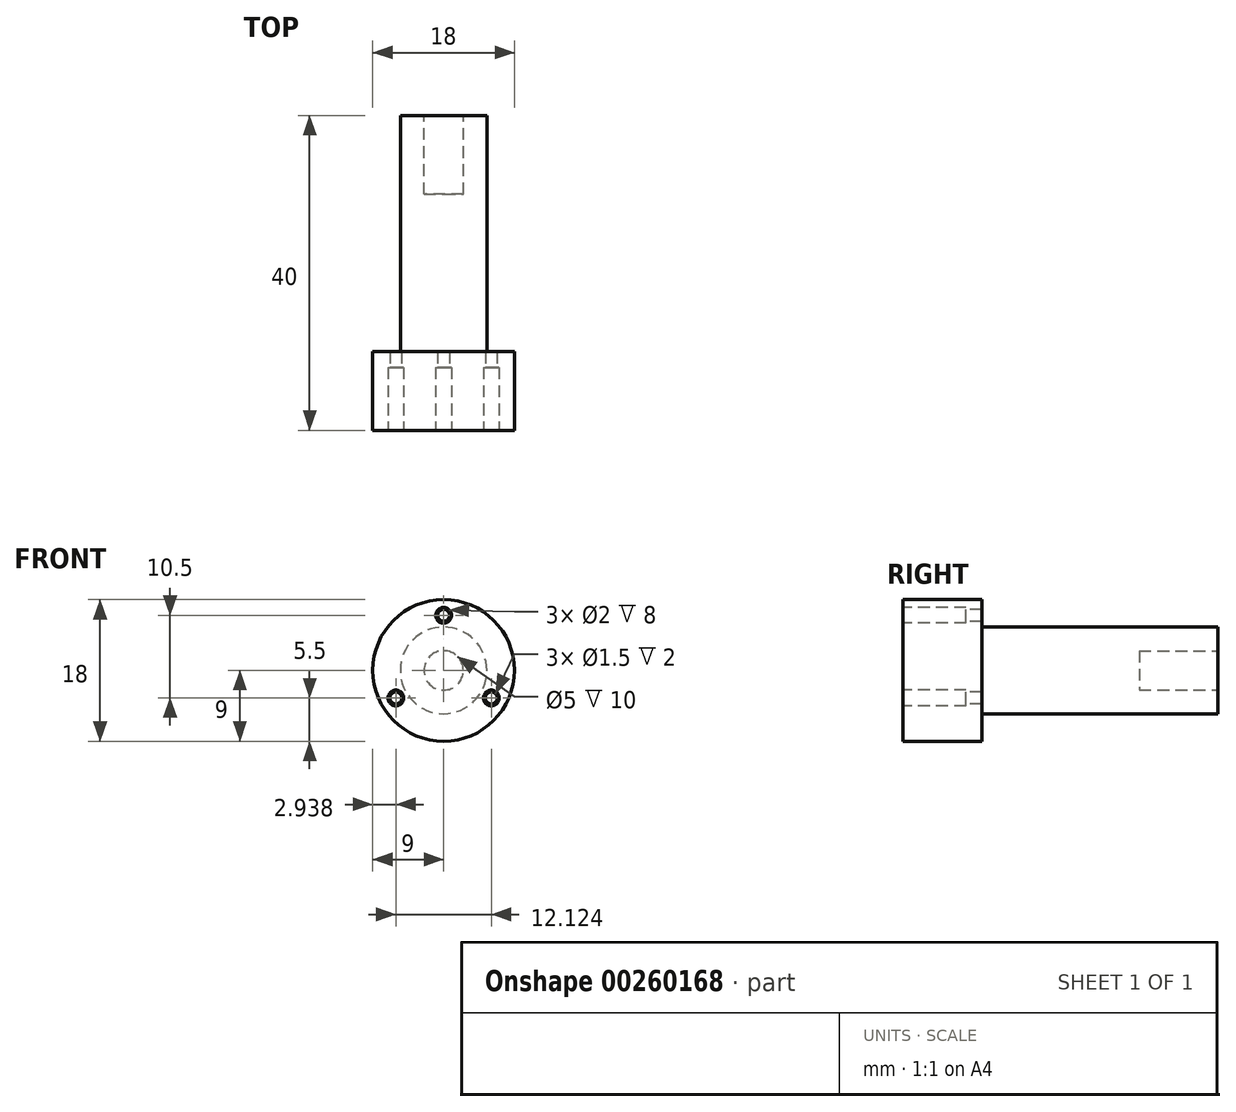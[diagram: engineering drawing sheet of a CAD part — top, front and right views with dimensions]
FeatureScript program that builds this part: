
annotation { "Feature Type Name" : "Feature", "Feature Type Description" : "" }
export const myFeature = defineFeature(function(context is Context, id is Id, definition is map)
    precondition{}
    {
        {
            var Q0;
            Q0=qCreatedBy(makeId("Front.planeOp"),FACE);
            var sketch = newSketch(context, id + "F0", { "sketchPlane" : qUnion([Q0])});
            skCircle(sketch, "E0", {"center": v(0, 0) * mm, "radius": 9 * mm});
            skSolve(sketch);
        }
        {
            var Q0;
            Q0=makeQuery(id+"F0.imprint","IMPRINT",FACE,{"disambiguationData":[TD([[makeQuery(id+"F0.imprint","IMPRINT",EDGE,{"derivedFrom":sQuery(id+"F0.wireOp",EDGE,"E0")}),1.0]])]});
            extrude(context, id + "F1", {"entities" : qUnion([Q0]), "endBound" : BoundingType.SYMMETRIC, "depth" : 40 * mm});
        }
        {
            var Q0;
            Q0=makeQuery(id+"F1.opExtrude","CAP_FACE",FACE,{"disambiguationData":[OSD([sQuery(id+"F0.wireOp",EDGE,"E0")])],"isStart":false});
            var sketch = newSketch(context, id + "F2", { "sketchPlane" : qUnion([Q0])});
            skArc(sketch, "E1", {"start": v(-1, 6.93) * mm, "mid": v(-6.06, 3.5) * mm, "end": v(-6.5, -2.6) * mm});
            skCircle(sketch, "E2", {"center": v(0, 7) * mm, "radius": 1 * mm});
            skCircle(sketch, "E3.1.0", {"center": v(-6.06, -3.5) * mm, "radius": 1 * mm});
            skCircle(sketch, "E3.2.0", {"center": v(6.06, -3.5) * mm, "radius": 1 * mm});
            skArc(sketch, "E4.trimOffspring", {"start": v(-5.5, -4.33) * mm, "mid": v(0, -7) * mm, "end": v(5.5, -4.33) * mm});
            skArc(sketch, "E5.trimOffspring", {"start": v(6.5, -2.6) * mm, "mid": v(6.06, 3.5) * mm, "end": v(1, 6.93) * mm});
            skCircle(sketch, "E6", {"center": v(-4, 0) * mm, "radius": 1.5 * mm});
            skCircle(sketch, "E7.MirrorC", {"center": v(4, 0) * mm, "radius": 1.5 * mm});
            skCircle(sketch, "E8", {"center": v(-6.06, -3.5) * mm, "radius": 0.75 * mm});
            skCircle(sketch, "E9.1.0", {"center": v(6.06, -3.5) * mm, "radius": 0.75 * mm});
            skCircle(sketch, "E9.2.0", {"center": v(0, 7) * mm, "radius": 0.75 * mm});
            skSolve(sketch);
        }
        {
            var Q0;
            {var subQ0=sQuery(id+"F2.wireOp",EDGE,"E2");var subQ1=makeQuery(id+"F2.imprint","INTERSECT",VERTEX,{"derivedFrom":[sQuery(id+"F2.wireOp",EDGE,"E1"),subQ0]});Q0=makeQuery(id+"F2.imprint","IMPRINT",FACE,{"disambiguationData":[TD([[makeQuery(id+"F2.imprint","IMPRINT",EDGE,{"disambiguationData":[TD([[subQ1,-1.0]])],"derivedFrom":subQ0}),1.0]])]});}
            var Q1;
            {var subQ0=sQuery(id+"F2.wireOp",EDGE,"E3.1.0");var subQ1=makeQuery(id+"F2.imprint","INTERSECT",VERTEX,{"derivedFrom":[sQuery(id+"F2.wireOp",EDGE,"E1"),subQ0]});Q1=makeQuery(id+"F2.imprint","IMPRINT",FACE,{"disambiguationData":[TD([[makeQuery(id+"F2.imprint","IMPRINT",EDGE,{"disambiguationData":[TD([[subQ1,1.0]])],"derivedFrom":subQ0}),1.0]])]});}
            var Q2;
            {var subQ0=sQuery(id+"F2.wireOp",EDGE,"E3.2.0");var subQ1=makeQuery(id+"F2.imprint","INTERSECT",VERTEX,{"derivedFrom":[subQ0,sQuery(id+"F2.wireOp",EDGE,"E4.trimOffspring")]});Q2=makeQuery(id+"F2.imprint","IMPRINT",FACE,{"disambiguationData":[TD([[makeQuery(id+"F2.imprint","IMPRINT",EDGE,{"disambiguationData":[TD([[subQ1,1.0]])],"derivedFrom":subQ0}),1.0]])]});}
            extrude(context, id + "F3", {"entities" : qUnion([Q0, Q1, Q2]), "operationType" : NewBodyOperationType.REMOVE, "oppositeDirection" : true, "depth" : 8 * mm});
        }
        {
            var Q0;
            Q0=makeQuery(id+"F1.opExtrude","CAP_FACE",FACE,{"disambiguationData":[OSD([sQuery(id+"F0.wireOp",EDGE,"E0")])],"isStart":true});
            var sketch = newSketch(context, id + "F4", { "sketchPlane" : qUnion([Q0])});
            skCircle(sketch, "E10", {"center": v(0, 0) * mm, "radius": 5.5 * mm});
            skSolve(sketch);
        }
        {
            var Q0;
            Q0=makeQuery(id+"F4.imprint","IMPRINT",FACE,{"disambiguationData":[TD([[makeQuery(id+"F4.imprint","IMPRINT",EDGE,{"derivedFrom":sQuery(id+"F4.wireOp",EDGE,"E10")}),-1.0]])]});
            extrude(context, id + "F5", {"entities" : qUnion([Q0]), "operationType" : NewBodyOperationType.REMOVE, "oppositeDirection" : true, "depth" : 30 * mm});
        }
        {
            var Q0;
            Q0=makeQuery(id+"F2.imprint","IMPRINT",FACE,{"disambiguationData":[TD([[makeQuery(id+"F2.imprint","IMPRINT",EDGE,{"derivedFrom":sQuery(id+"F2.wireOp",EDGE,"E8")}),1.0]])]});
            var Q1;
            Q1=makeQuery(id+"F2.imprint","IMPRINT",FACE,{"disambiguationData":[TD([[makeQuery(id+"F2.imprint","IMPRINT",EDGE,{"derivedFrom":sQuery(id+"F2.wireOp",EDGE,"E9.2.0")}),1.0]])]});
            var Q2;
            Q2=makeQuery(id+"F2.imprint","IMPRINT",FACE,{"disambiguationData":[TD([[makeQuery(id+"F2.imprint","IMPRINT",EDGE,{"derivedFrom":sQuery(id+"F2.wireOp",EDGE,"E9.1.0")}),1.0]])]});
            extrude(context, id + "F6", {"entities" : qUnion([Q0, Q1, Q2]), "operationType" : NewBodyOperationType.REMOVE, "oppositeDirection" : true, "depth" : 10 * mm});
        }
        {
            var Q0;
            Q0=makeQuery(id+"F1.opExtrude","CAP_FACE",FACE,{"disambiguationData":[OSD([sQuery(id+"F0.wireOp",EDGE,"E0")])],"isStart":true});
            var sketch = newSketch(context, id + "F7", { "sketchPlane" : qUnion([Q0])});
            skCircle(sketch, "E11", {"center": v(0, 0) * mm, "radius": 2.5 * mm});
            skSolve(sketch);
        }
        {
            var Q0;
            Q0=makeQuery(id+"F7.imprint","IMPRINT",FACE,{"disambiguationData":[TD([[makeQuery(id+"F7.imprint","IMPRINT",EDGE,{"derivedFrom":sQuery(id+"F7.wireOp",EDGE,"E11")}),1.0]])]});
            extrude(context, id + "F8", {"entities" : qUnion([Q0]), "operationType" : NewBodyOperationType.REMOVE, "oppositeDirection" : true, "depth" : 10 * mm});
        }
    });
